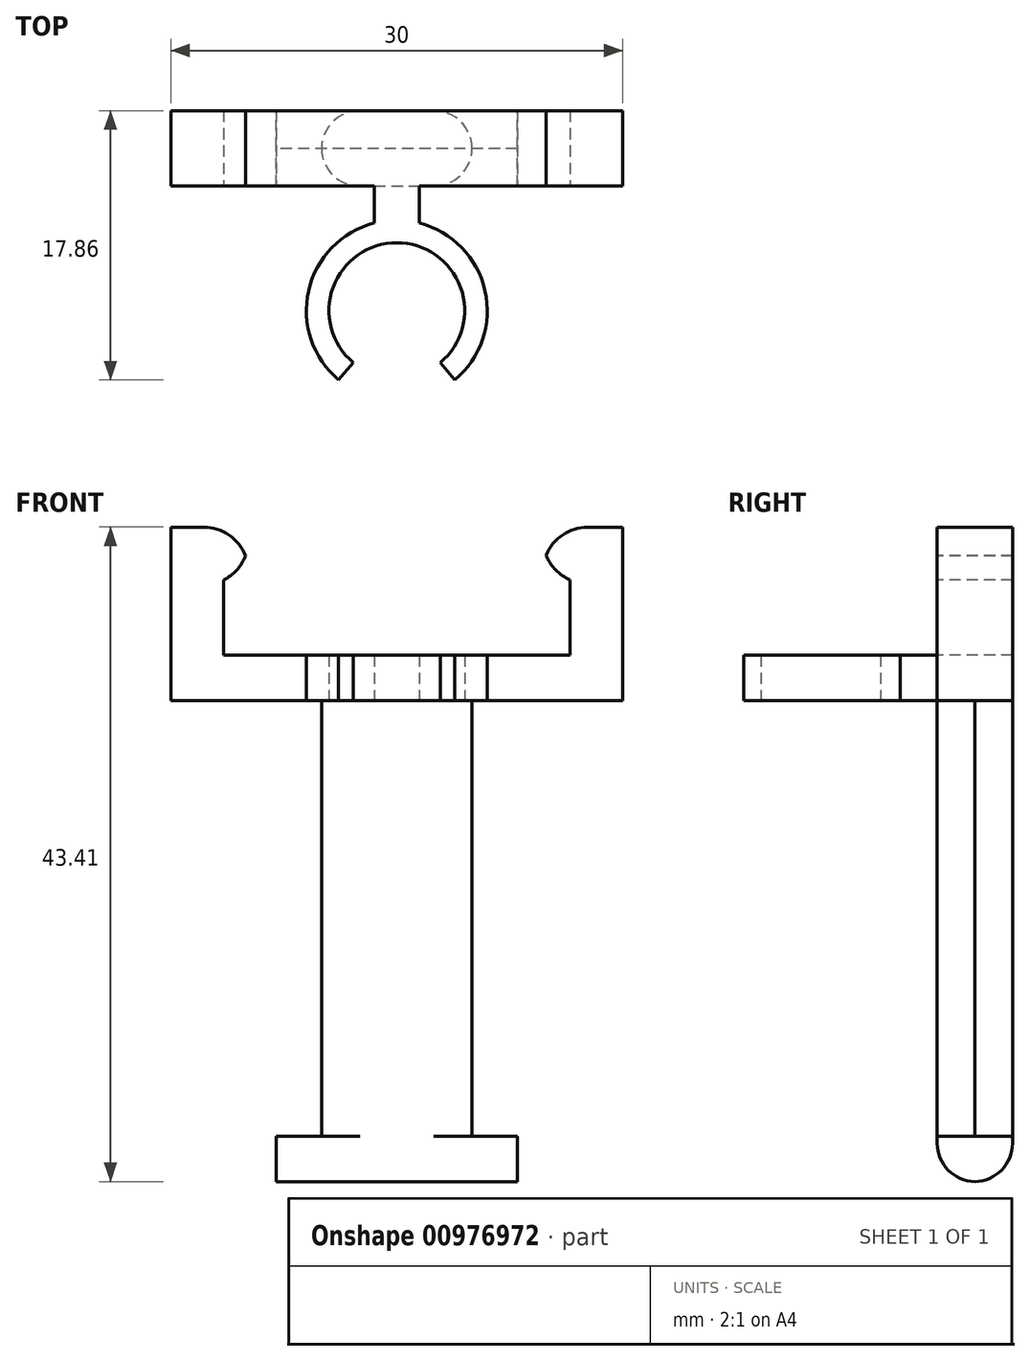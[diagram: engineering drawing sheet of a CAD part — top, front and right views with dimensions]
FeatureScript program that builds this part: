
annotation { "Feature Type Name" : "Feature", "Feature Type Description" : "" }
export const myFeature = defineFeature(function(context is Context, id is Id, definition is map)
    precondition{}
    {
        {
            var Q0;
            Q0=qCreatedBy(makeId("Top.planeOp"),FACE);
            var sketch = newSketch(context, id + "F0", { "sketchPlane" : qUnion([Q0])});
            skArc(sketch, "E0", {"start": v(2.9, -3.45) * mm, "mid": v(0, 4.5) * mm, "end": v(-2.9, -3.45) * mm});
            skLineSegment(sketch, "E1", {"start": v(3.86, -4.6) * mm, "end": v(3.86, -4.6) * mm});
            skLineSegment(sketch, "E2", {"start": v(-2.9, -3.45) * mm, "end": v(-3.86, -4.6) * mm});
            skLineSegment(sketch, "E3.MirrorCS", {"start": v(2.9, -3.45) * mm, "end": v(3.86, -4.6) * mm});
            skArc(sketch, "E4.trimOffspring", {"start": v(3.86, -4.6) * mm, "mid": v(5.97, 0.58) * mm, "end": v(2.9, 5.26) * mm});
            skArc(sketch, "E5.trimOffspring", {"start": v(2.9, 5.26) * mm, "mid": v(2.21, 5.58) * mm, "end": v(1.5, 5.8) * mm});
            skLineSegment(sketch, "E6", {"start": v(-1.5, 5.8) * mm, "end": v(-1.5, 8.26) * mm});
            skLineSegment(sketch, "E7.MirrorCS", {"start": v(1.5, 5.8) * mm, "end": v(1.5, 8.26) * mm});
            skLineSegment(sketch, "E8", {"start": v(-1.5, 8.26) * mm, "end": v(1.5, 8.26) * mm});
            skPoint(sketch, "E9.start.orphan", {"position": v(0, 5.26) * mm});
            skArc(sketch, "E10.trimOffspring", {"start": v(-1.5, 5.8) * mm, "mid": v(-5.85, 1.33) * mm, "end": v(-3.86, -4.6) * mm});
            skSolve(sketch);
        }
        {
            var Q0;
            Q0=makeQuery(id+"F0.imprint","IMPRINT",FACE,{"disambiguationData":[TD([[makeQuery(id+"F0.imprint","IMPRINT",EDGE,{"derivedFrom":sQuery(id+"F0.wireOp",EDGE,"E0")}),-1.0]])]});
            extrude(context, id + "F1", {"entities" : qUnion([Q0]), "depth" : 3 * mm, "offsetDistance" : 25.4 * mm});
        }
        {
            var Q0;
            Q0=makeQuery(id+"F1.opExtrude","SWEPT_FACE",FACE,{"disambiguationData":[OSD([sQuery(id+"F0.wireOp",EDGE,"E8")])]});
            var sketch = newSketch(context, id + "F2", { "sketchPlane" : qUnion([Q0])});
            skLineSegment(sketch, "E11", {"start": v(-5, 0) * mm, "end": v(-15, 0) * mm});
            skLineSegment(sketch, "E12.left", {"start": v(-15, 11.5) * mm, "end": v(-15, 0) * mm});
            skPoint(sketch, "E12.middle", {"position": v(0, 0) * mm});
            skLineSegment(sketch, "E13", {"start": v(-15, 11.5) * mm, "end": v(-9.69, 11.5) * mm});
            skLineSegment(sketch, "E14", {"start": v(-15, 3) * mm, "end": v(-15, 8) * mm});
            skLineSegment(sketch, "E15", {"start": v(-15, 8) * mm, "end": v(-15, 11.5) * mm});
            skLineSegment(sketch, "E16", {"start": v(-11.5, 8) * mm, "end": v(-9.69, 8) * mm});
            skLineSegment(sketch, "E17", {"start": v(-11.5, 8) * mm, "end": v(-11.5, 3) * mm});
            skLineSegment(sketch, "E18", {"start": v(-11.5, 3) * mm, "end": v(0, 3) * mm});
            skLineSegment(sketch, "E19", {"start": v(-13.2, 11.5) * mm, "end": v(-9.69, 11.5) * mm});
            skLineSegment(sketch, "E20", {"start": v(-9.69, 11.5) * mm, "end": v(-9.69, 8) * mm});
            skPoint(sketch, "E21.orphan", {"position": v(0, 8) * mm});
            skPoint(sketch, "E22.start.orphan", {"position": v(0, 1.5) * mm});
            skPoint(sketch, "E23.orphan", {"position": v(15, 11.5) * mm});
            skPoint(sketch, "E12.top.start.orphan", {"position": v(-15, -11.5) * mm});
            skLineSegment(sketch, "E24.MirrorCS", {"start": v(11.5, 3) * mm, "end": v(0, 3) * mm});
            skLineSegment(sketch, "E25.MirrorCS", {"start": v(5, 0) * mm, "end": v(15, 0) * mm});
            skLineSegment(sketch, "E26.MirrorCS", {"start": v(15, 3) * mm, "end": v(15, 8) * mm});
            skLineSegment(sketch, "E27.MirrorCS", {"start": v(11.5, 8) * mm, "end": v(11.5, 3) * mm});
            skLineSegment(sketch, "E28.MirrorCS", {"start": v(15, 11.5) * mm, "end": v(15, 0) * mm});
            skLineSegment(sketch, "E29.MirrorCS", {"start": v(15, 11.5) * mm, "end": v(9.83, 11.5) * mm});
            skLineSegment(sketch, "E30.MirrorCS", {"start": v(9.83, 11.5) * mm, "end": v(9.83, 8) * mm});
            skLineSegment(sketch, "E31.MirrorCS", {"start": v(11.5, 8) * mm, "end": v(9.83, 8) * mm});
            skPoint(sketch, "E32.visualSharp", {"position": v(-9.69, 11.5) * mm});
            skLineSegment(sketch, "E32.filletArc", {"start": v(-9.69, 11.5) * mm, "end": v(-9.69, 11.5) * mm});
            skLineSegment(sketch, "E33", {"start": v(5, -28.9) * mm, "end": v(5, 0) * mm});
            skLineSegment(sketch, "E34", {"start": v(8, -31.9) * mm, "end": v(8, -28.9) * mm});
            skLineSegment(sketch, "E35", {"start": v(8, -28.9) * mm, "end": v(5, -28.9) * mm});
            skLineSegment(sketch, "E36.MirrorCS", {"start": v(-8, -31.9) * mm, "end": v(-8, -28.9) * mm});
            skLineSegment(sketch, "E37.MirrorCS", {"start": v(-8, -28.9) * mm, "end": v(-5, -28.9) * mm});
            skPoint(sketch, "E38.MirrorCS.end.orphan", {"position": v(-5, -10) * mm});
            skPoint(sketch, "E38.MirrorCS.start.orphan", {"position": v(0, -10) * mm});
            skPoint(sketch, "E39.end.orphan", {"position": v(0, -28.9) * mm});
            skLineSegment(sketch, "E40", {"start": v(-8, -31.9) * mm, "end": v(8, -31.9) * mm});
            skLineSegment(sketch, "E41", {"start": v(-5, 0) * mm, "end": v(-5, -28.9) * mm});
            skSolve(sketch);
        }
        {
            var Q0;
            Q0 = qSketchRegion(id + "F2", true);
            extrude(context, id + "F3", {"entities" : qUnion([Q0]), "operationType" : NewBodyOperationType.ADD, "depth" : 5 * mm, "offsetDistance" : 25.4 * mm});
        }
        {
            var Q0;
            Q0=makeQuery(id+"F3.opExtrude","SWEPT_EDGE",EDGE,{"disambiguationData":[OSD([sQuery(id+"F2.wireOp",EDGE,"E19"),sQuery(id+"F2.wireOp",EDGE,"E20")])]});
            var Q1;
            Q1=makeQuery(id+"F3.opExtrude","SWEPT_EDGE",EDGE,{"disambiguationData":[OSD([sQuery(id+"F2.wireOp",EDGE,"E29.MirrorCS"),sQuery(id+"F2.wireOp",EDGE,"E30.MirrorCS")])]});
            var Q2;
            Q2=makeQuery(id+"F3.opExtrude","SWEPT_EDGE",EDGE,{"disambiguationData":[OSD([sQuery(id+"F2.wireOp",EDGE,"E16"),sQuery(id+"F2.wireOp",EDGE,"E20")])]});
            var Q3;
            Q3=makeQuery(id+"F3.opExtrude","SWEPT_EDGE",EDGE,{"disambiguationData":[OSD([sQuery(id+"F2.wireOp",EDGE,"E30.MirrorCS"),sQuery(id+"F2.wireOp",EDGE,"E31.MirrorCS")])]});
            fillet(context, id + "F4", {"entities" : qUnion([Q0, Q1, Q2, Q3]), "radius" : 3 * mm, "tangentPropagation" : true, "allowEdgeOverflow" : false});
        }
        {
            var Q0;
            Q0=makeQuery(id+"F3.opExtrude","CAP_EDGE",EDGE,{"disambiguationData":[OSD([sQuery(id+"F2.wireOp",EDGE,"E41")])],"isStart":false});
            var Q1;
            Q1=makeQuery(id+"F3.opExtrude","CAP_EDGE",EDGE,{"disambiguationData":[OSD([sQuery(id+"F2.wireOp",EDGE,"E41")])],"isStart":true});
            var Q2;
            Q2=makeQuery(id+"F3.opExtrude","CAP_EDGE",EDGE,{"disambiguationData":[OSD([sQuery(id+"F2.wireOp",EDGE,"E33")])],"isStart":true});
            var Q3;
            Q3=makeQuery(id+"F3.opExtrude","CAP_EDGE",EDGE,{"disambiguationData":[OSD([sQuery(id+"F2.wireOp",EDGE,"E33")])],"isStart":false});
            var Q4;
            Q4=makeQuery(id+"F3.opExtrude","CAP_EDGE",EDGE,{"disambiguationData":[OSD([sQuery(id+"F2.wireOp",EDGE,"E40")])],"isStart":true});
            var Q5;
            Q5=makeQuery(id+"F3.opExtrude","CAP_EDGE",EDGE,{"disambiguationData":[OSD([sQuery(id+"F2.wireOp",EDGE,"E40")])],"isStart":false});
            fillet(context, id + "F5", {"entities" : qUnion([Q0, Q1, Q2, Q3, Q4, Q5]), "radius" : 2.54 * mm, "tangentPropagation" : true, "allowEdgeOverflow" : false});
        }
    });
